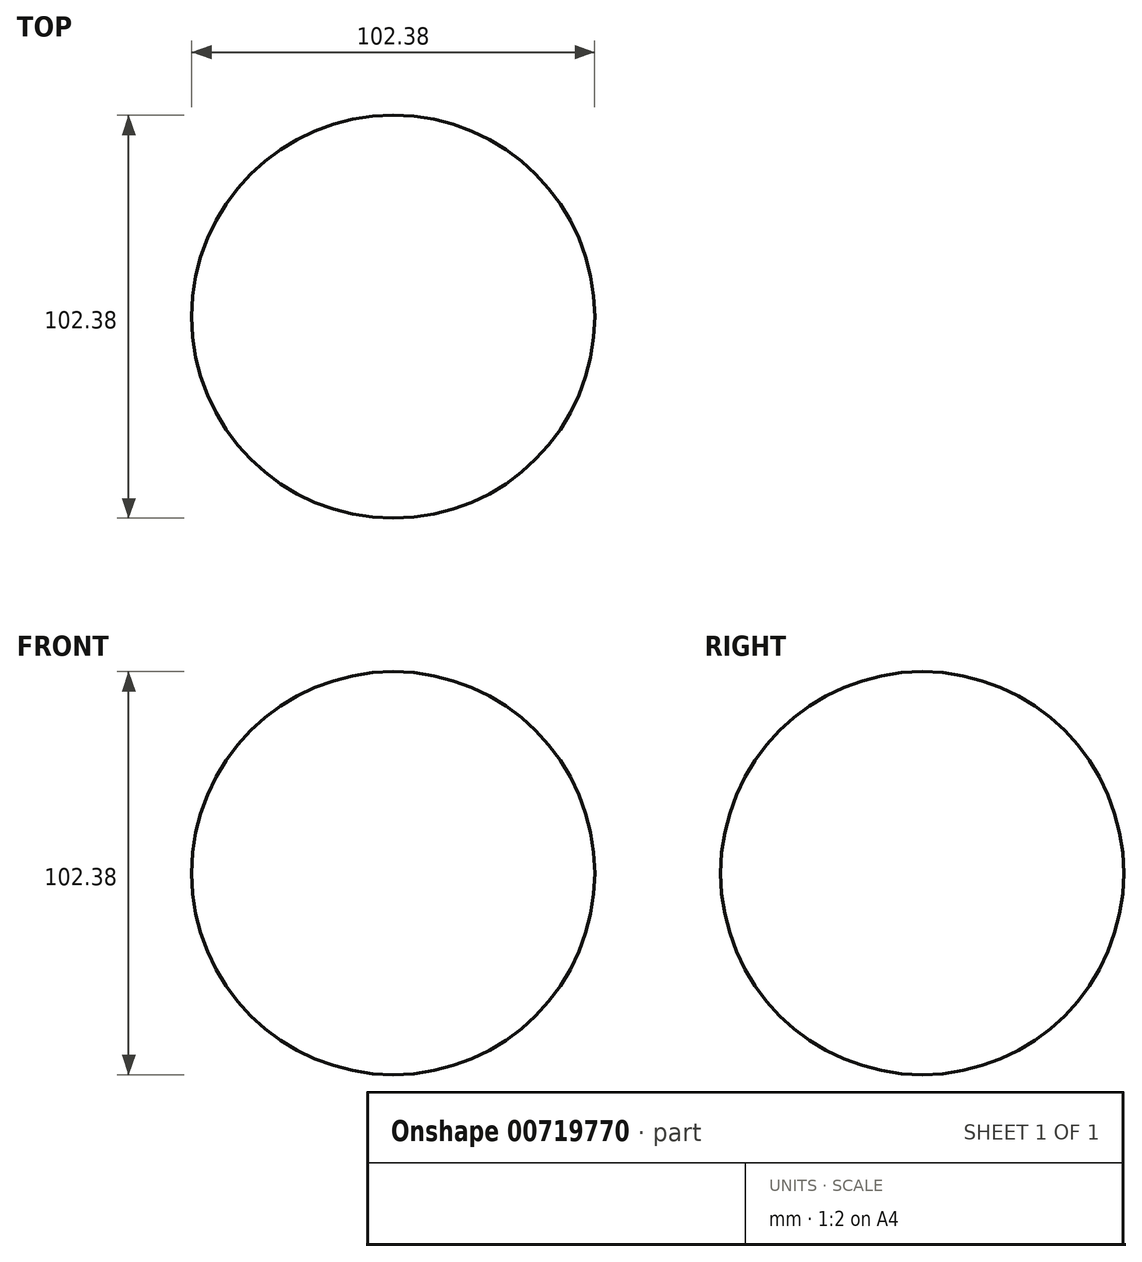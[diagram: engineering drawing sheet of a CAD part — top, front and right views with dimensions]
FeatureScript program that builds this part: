
annotation { "Feature Type Name" : "Feature", "Feature Type Description" : "" }
export const myFeature = defineFeature(function(context is Context, id is Id, definition is map)
    precondition{}
    {
        {
            var Q0;
            Q0=qCreatedBy(makeId("Front.planeOp"),FACE);
            var sketch = newSketch(context, id + "F0", { "sketchPlane" : qUnion([Q0])});
            skArc(sketch, "E0", {"start": v(51.2, 0) * mm, "mid": v(0, 51.2) * mm, "end": v(-51.2, 0) * mm});
            skSolve(sketch);
        }
        {
            var Q0;
            Q0=qCreatedBy(makeId("Front.planeOp"),FACE);
            var sketch = newSketch(context, id + "F1", { "sketchPlane" : qUnion([Q0])});
            skLineSegment(sketch, "E1", {"start": v(-51.2, 0) * mm, "end": v(51.2, 0) * mm});
            skSolve(sketch);
        }
        {
            var Q0;
            Q0=sQuery(id+"F0.wireOp",EDGE,"E0");
            var Q1;
            Q1=sQuery(id+"F1.wireOp",EDGE,"E1");
            revolve(context, id + "F2", {"bodyType" : ToolBodyType.SURFACE, "surfaceOperationType" : NewSurfaceOperationType.NEW, "surfaceEntities" : qUnion([Q0]), "axis" : qUnion([Q1]), "revolveType" : RevolveType.FULL});
        }
    });
